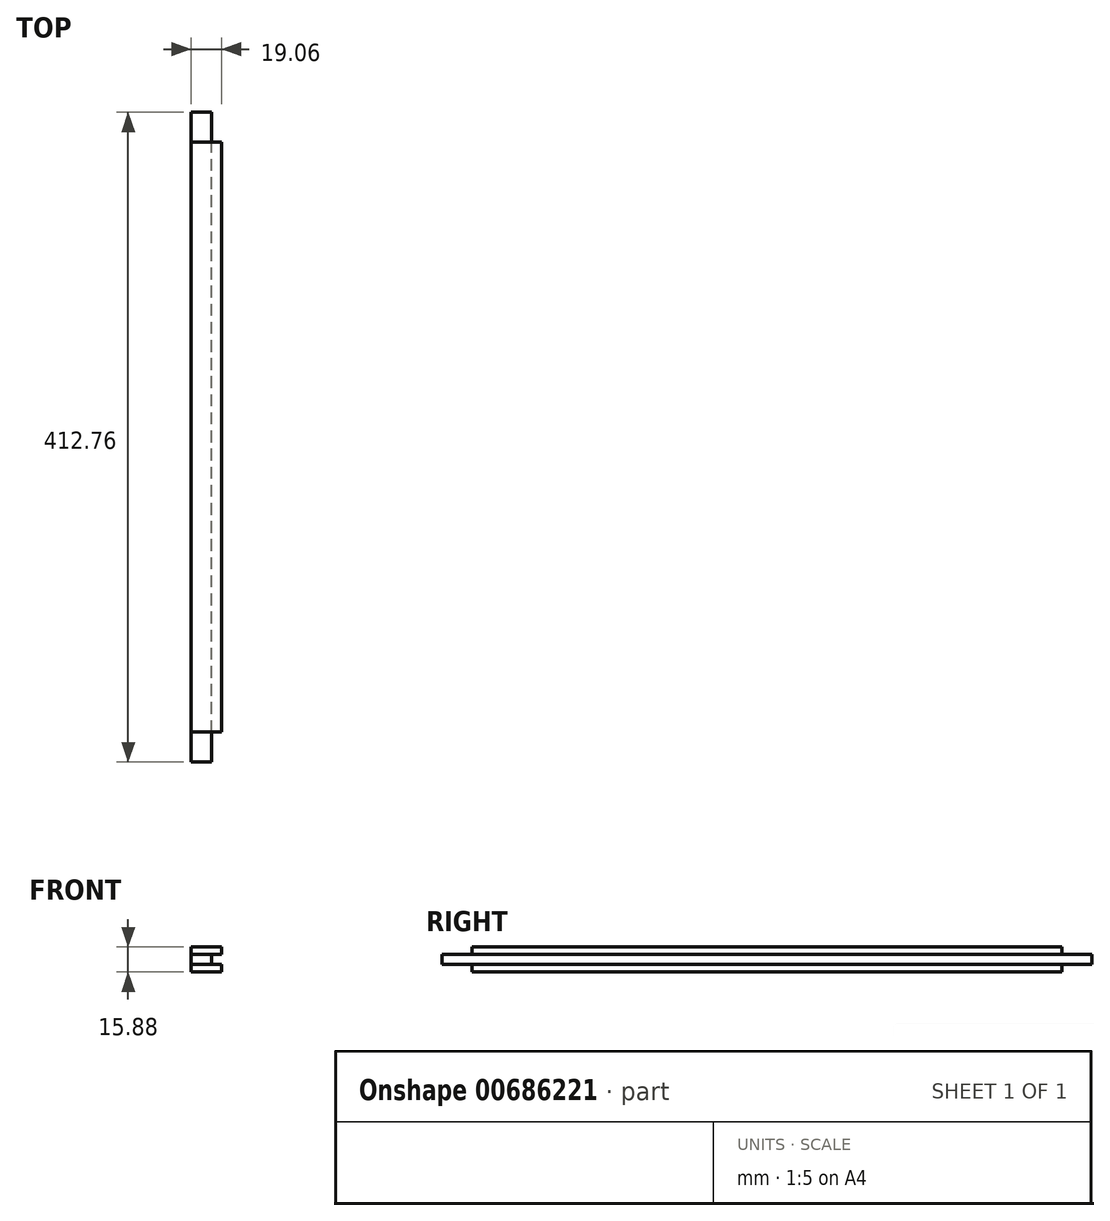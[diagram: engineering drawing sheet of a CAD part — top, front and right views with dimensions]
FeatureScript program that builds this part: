
annotation { "Feature Type Name" : "Feature", "Feature Type Description" : "" }
export const myFeature = defineFeature(function(context is Context, id is Id, definition is map)
    precondition{}
    {
        {
            var Q0;
            Q0=qCreatedBy(makeId("Front.planeOp"),FACE);
            var sketch = newSketch(context, id + "F0", { "sketchPlane" : qUnion([Q0])});
            skLineSegment(sketch, "E0.bottom", {"start": v(-9.53, 7.94) * mm, "end": v(9.52, 7.94) * mm});
            skLineSegment(sketch, "E0.top", {"start": v(-9.53, -7.94) * mm, "end": v(9.52, -7.94) * mm});
            skLineSegment(sketch, "E0.left", {"start": v(-9.53, 7.94) * mm, "end": v(-9.53, -7.94) * mm});
            skLineSegment(sketch, "E0.right", {"start": v(9.52, 7.94) * mm, "end": v(9.52, 3.18) * mm});
            skPoint(sketch, "E0.middle", {"position": v(0, 0) * mm});
            skLineSegment(sketch, "E1", {"start": v(9.52, 3.18) * mm, "end": v(3.17, 3.18) * mm});
            skLineSegment(sketch, "E2", {"start": v(3.17, 3.18) * mm, "end": v(3.17, -3.18) * mm});
            skLineSegment(sketch, "E3", {"start": v(3.17, -3.18) * mm, "end": v(9.52, -3.17) * mm});
            skLineSegment(sketch, "E4", {"start": v(0, 0) * mm, "end": v(3.17, 0) * mm, "construction": true});
            skLineSegment(sketch, "E5.trimOffspring", {"start": v(9.52, -3.17) * mm, "end": v(9.52, -7.94) * mm});
            skSolve(sketch);
        }
        {
            var Q0;
            Q0=qSketchRegion(id+"F0",true);
            extrude(context, id + "F1", {"entities" : qUnion([Q0]), "endBound" : BoundingType.SYMMETRIC, "depth" : 412.75 * mm, "offsetDistance" : 25.4 * mm});
        }
        {
            var Q0;
            Q0=qCreatedBy(makeId("Right.planeOp"),FACE);
            var sketch = newSketch(context, id + "F2", { "sketchPlane" : qUnion([Q0])});
            skLineSegment(sketch, "E6.bottom", {"start": v(-187.33, -3.17) * mm, "end": v(-206.38, -3.17) * mm, "construction": true});
            skLineSegment(sketch, "E6.top", {"start": v(-187.33, 3.18) * mm, "end": v(-206.38, 3.18) * mm, "construction": true});
            skLineSegment(sketch, "E6.left", {"start": v(-187.33, -3.17) * mm, "end": v(-187.33, 3.18) * mm, "construction": true});
            skLineSegment(sketch, "E6.right", {"start": v(-206.38, -3.17) * mm, "end": v(-206.38, 3.18) * mm, "construction": true});
            skLineSegment(sketch, "E7", {"start": v(0, 21.45) * mm, "end": v(0, -22.74) * mm, "construction": true});
            skLineSegment(sketch, "E8.MirrorCS", {"start": v(206.38, -3.17) * mm, "end": v(206.38, 3.18) * mm, "construction": true});
            skLineSegment(sketch, "E9.MirrorCS", {"start": v(187.33, -3.17) * mm, "end": v(187.33, 3.18) * mm, "construction": true});
            skLineSegment(sketch, "E10.MirrorCS", {"start": v(187.33, 3.18) * mm, "end": v(206.38, 3.18) * mm, "construction": true});
            skLineSegment(sketch, "E11.MirrorCS", {"start": v(187.33, -3.17) * mm, "end": v(206.38, -3.17) * mm, "construction": true});
            skLineSegment(sketch, "E12.bottom", {"start": v(-187.33, 3.18) * mm, "end": v(-206.38, 3.18) * mm});
            skLineSegment(sketch, "E12.top", {"start": v(-187.33, 7.94) * mm, "end": v(-206.38, 7.94) * mm});
            skLineSegment(sketch, "E12.left", {"start": v(-187.33, 3.18) * mm, "end": v(-187.33, 7.94) * mm});
            skLineSegment(sketch, "E12.right", {"start": v(-206.38, 3.18) * mm, "end": v(-206.38, 7.94) * mm});
            skLineSegment(sketch, "E13.bottom", {"start": v(-187.33, -3.17) * mm, "end": v(-206.38, -3.17) * mm});
            skLineSegment(sketch, "E13.top", {"start": v(-187.33, -7.94) * mm, "end": v(-206.38, -7.94) * mm});
            skLineSegment(sketch, "E13.left", {"start": v(-187.33, -3.17) * mm, "end": v(-187.33, -7.94) * mm});
            skLineSegment(sketch, "E13.right", {"start": v(-206.38, -3.17) * mm, "end": v(-206.38, -7.94) * mm});
            skLineSegment(sketch, "E14.bottom", {"start": v(187.33, 3.18) * mm, "end": v(206.38, 3.18) * mm});
            skLineSegment(sketch, "E14.top", {"start": v(187.33, 7.94) * mm, "end": v(206.38, 7.94) * mm});
            skLineSegment(sketch, "E14.left", {"start": v(187.33, 3.18) * mm, "end": v(187.33, 7.94) * mm});
            skLineSegment(sketch, "E14.right", {"start": v(206.38, 3.18) * mm, "end": v(206.38, 7.94) * mm});
            skLineSegment(sketch, "E15.bottom", {"start": v(187.33, -3.17) * mm, "end": v(206.38, -3.17) * mm});
            skLineSegment(sketch, "E15.top", {"start": v(187.33, -7.94) * mm, "end": v(206.38, -7.94) * mm});
            skLineSegment(sketch, "E15.left", {"start": v(187.33, -3.17) * mm, "end": v(187.33, -7.94) * mm});
            skLineSegment(sketch, "E15.right", {"start": v(206.38, -3.17) * mm, "end": v(206.38, -7.94) * mm});
            skSolve(sketch);
        }
        {
            var Q0;
            Q0=qSketchRegion(id+"F2",true);
            extrude(context, id + "F3", {"entities" : qUnion([Q0]), "operationType" : NewBodyOperationType.REMOVE, "endBound" : BoundingType.THROUGH_ALL, "oppositeDirection" : true, "depth" : 25.4 * mm, "offsetDistance" : 25.4 * mm, "hasSecondDirection" : true, "secondDirectionBound" : SecondDirectionBoundingType.THROUGH_ALL, "secondDirectionOppositeDirection" : false, "secondDirectionDepth" : 25.4 * mm});
        }
    });
